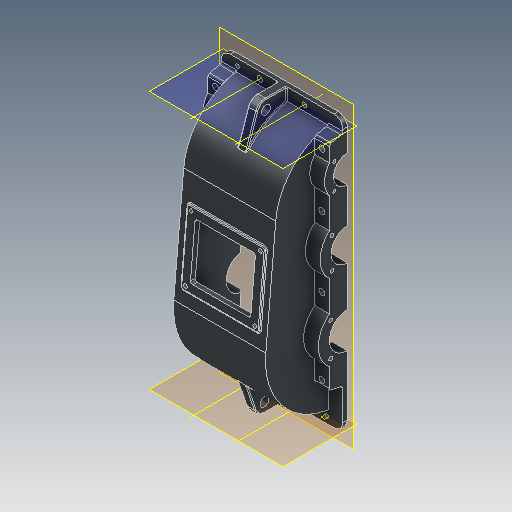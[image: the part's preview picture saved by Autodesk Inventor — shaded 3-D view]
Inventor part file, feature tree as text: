
AUTODESK INVENTOR PART (.ipt)
format: ipt  version: 2025 (Build 290162000, 162)  size: 666,624 bytes
history: native  units: mm
features: reference x41, other x28, sketch x13, extrude x7, hole x5, thread x5, plane x4, fillet x2, revolve x2, shell x1, mirror x1, chamfer x1, projected_geometry x1
ambient origin geometry x8: Origin, YZ Plane, XZ Plane, XY Plane, X Axis, Y Axis, Z Axis, Center Point
bodies: 实体1 (feature_tree)
feature tree (111):
  plane  "工作平面1"
  extrude  "拉伸1"  Depth=10.0mm
  extrude  "拉伸2"  Depth=80.0mm
  shell  "抽壳1"  Thickness=206.0mm
  extrude  "拉伸3"  Depth=8.0mm
  extrude  "拉伸4"  Depth=40.0mm
  mirror  "镜像1"
  hole  "孔1"  [1 undecoded]
  hole  "孔3"  [1 undecoded]
  hole  "孔4"  [1 undecoded]
  hole  "孔5"  [1 undecoded]
  hole  "孔6"  [1 undecoded]
  sketch  "草图13"  dims[d45=8.376mm d46=28.0mm d47=4.0mm d48=2.0mm d49=90.0deg d50=30.0mm d51=120.0deg]
  extrude  "拉伸5"  Depth=8.0mm
  extrude  "拉伸6"  Depth=8.0mm
  fillet  "圆角2"  Radius=120.0mm
  thread  "螺纹1"  [1 undecoded]
  thread  "螺纹2"  [1 undecoded]
  thread  "螺纹3"  [1 undecoded]
  thread  "螺纹4"  [1 undecoded]
  extrude  "拉伸7"  Depth=8.0mm TaperAngle=0.0deg
  fillet  "圆角3"  Radius=20.0mm
  plane  "工作平面2"
  revolve  "旋转1"  [1 undecoded]
  plane  "工作平面3"
  plane  "工作平面4"
  revolve  "旋转2"  [1 undecoded]
  thread  "螺纹5"  [1 undecoded]
  chamfer  "倒角1"  Distance=20.0mm
  sketch  "草图1"  dims[d0=10.0mm d1=0.0mm d2=300.0mm]
  reference  "参考1"
  reference  "参考2"
  reference  "参考3"
  reference  "参考4"
  reference  "参考5"
  reference  "参考6"
  sketch  "草图2"  dims[d3=270.0mm d4=80.0mm d5=206.0mm d6=0.0mm]
  reference  "参考7"
  reference  "参考8"
  reference  "参考9"
  sketch  "草图3"  dims[d7=8.0mm d8=8.0mm]
  reference  "参考11"
  reference  "参考12"
  reference  "参考13"
  sketch  "草图4"  dims[d9=0.0mm d10=0.0mm d11=40.0mm]
  projected_geometry  "投影回路1"
  reference  "参考14"
  reference  "参考15"
  reference  "参考16"
  reference  "参考17"
  reference  "参考18"
  sketch  "草图5"  dims[d12=29.408798mm d13=29.408798mm]
  reference  "参考19"
  reference  "参考20"
  reference  "参考21"
  reference  "参考22"
  reference  "参考23"
  reference  "参考24"
  reference  "参考25"
  reference  "参考26"
  sketch  "草图9"  dims[d14=36.0mm d15=0.0mm d16=5.0mm]
  reference  "参考33"
  reference  "参考34"
  sketch  "草图10"  dims[d17=13.0mm d18=6.0mm d19=4.0mm d20=2.0mm d21=90.0deg d22=8.0mm d23=20.594885mm]
  reference  "参考35"
  reference  "参考36"
  sketch  "草图11"  dims[d31=6.647mm d32=28.0mm d33=4.0mm d34=2.0mm d35=90.0deg d36=30.0mm d37=120.0deg]
  reference  "参考37"
  reference  "参考38"
  reference  "参考39"
  reference  "参考40"
  sketch  "草图12"  dims[d38=6.647mm d39=28.0mm d40=4.0mm d41=2.0mm d42=90.0deg d43=30.0mm d44=120.0deg]
  reference  "参考41"
  reference  "参考42"
  reference  "参考43"
  reference  "参考44"
  sketch  "草图14"  dims[d52=8.376mm d53=28.0mm d54=4.0mm d55=2.0mm d56=90.0deg d57=30.0mm d58=120.0deg d59=175.0mm]
  other  "工作轴1"
  other  "工作轴2"
  sketch  "草图15"  dims[d60=160.0mm d61=5.0mm]
  reference  "参考45"
  reference  "参考46"
  other  "工作轴3"
  other  "工作轴4"
  sketch  "草图16"  dims[d62=155.0mm d63=140.0mm d64=8.0mm d65=135.0mm d66=120.0mm d67=5.0mm d68=3.0mm d69=0.0mm d70=3.0mm d71=0.0mm d72=2.0mm d73=11.0mm d74=0.0mm d75=20.0mm d76=0.0mm d77=11.0mm d78=0.0mm d79=20.0mm d80=0.0mm d81=22.0mm d82=20.0mm d83=142.282327mm d84=162.282327mm d85=90.0mm d86=20.0mm d87=0.0mm d88=2.0mm d91=166.895756mm d92=90.0mm d93=22.0mm d94=186.895756mm d95=20.0mm d96=28.0mm d97=28.0mm d98=90.0deg d99=90.0deg d100=10.0mm d101=10.0mm d102=0.0mm d103=8.0mm d104=2.0mm d105=45.0deg]
  reference  "参考47"
  reference  "参考48"
  other  "齿轮箱.iam"
  other  "下半箱体:1"
  other  "低速齿轮:1"
  other  "正齿轮:1"
  other  "正齿轮2:1"
  other  "高速齿轮:1"
  other  "高速轴:1"
  other  "轴承:2"
  other  "滚动轴承 GB/T 276-1994 60000 和 160000 型 6206:1"
  other  "中间轴:1"
  other  "滚动轴承 GB/T 276-1994 60000 和 160000 型 6306:1"
  other  "低速轴:1"
  other  "滚动轴承 GB/T 276-1994 60000 和 160000 型 6010:1"
  other  "高速轴承透盖"
  other  "高速轴承闷盖"
  other  "中间轴承闷盖1"
  other  "低速轴承透盖"
  other  "中间轴承闷盖2"
  other  "低速轴承闷盖"
  other  "定位销:1"
  other  "定位销:2"
  parser-record x1  (decoder bookkeeping rows leaked as tree rows — omitted from the tree; the rows remain in map.json)
  other  "齿轮箱1.iam"
  other  "<userpath>\Desktop\Inventor files\齿轮箱.iam"
note: 12 required parameter values undecoded (feature->parameter linkage not recoverable at this tier; creation-order binding heuristic only, values carry confidence <= 0.55)
note: 1 file-system path scrubbed to <path> (originals preserved in map.json)